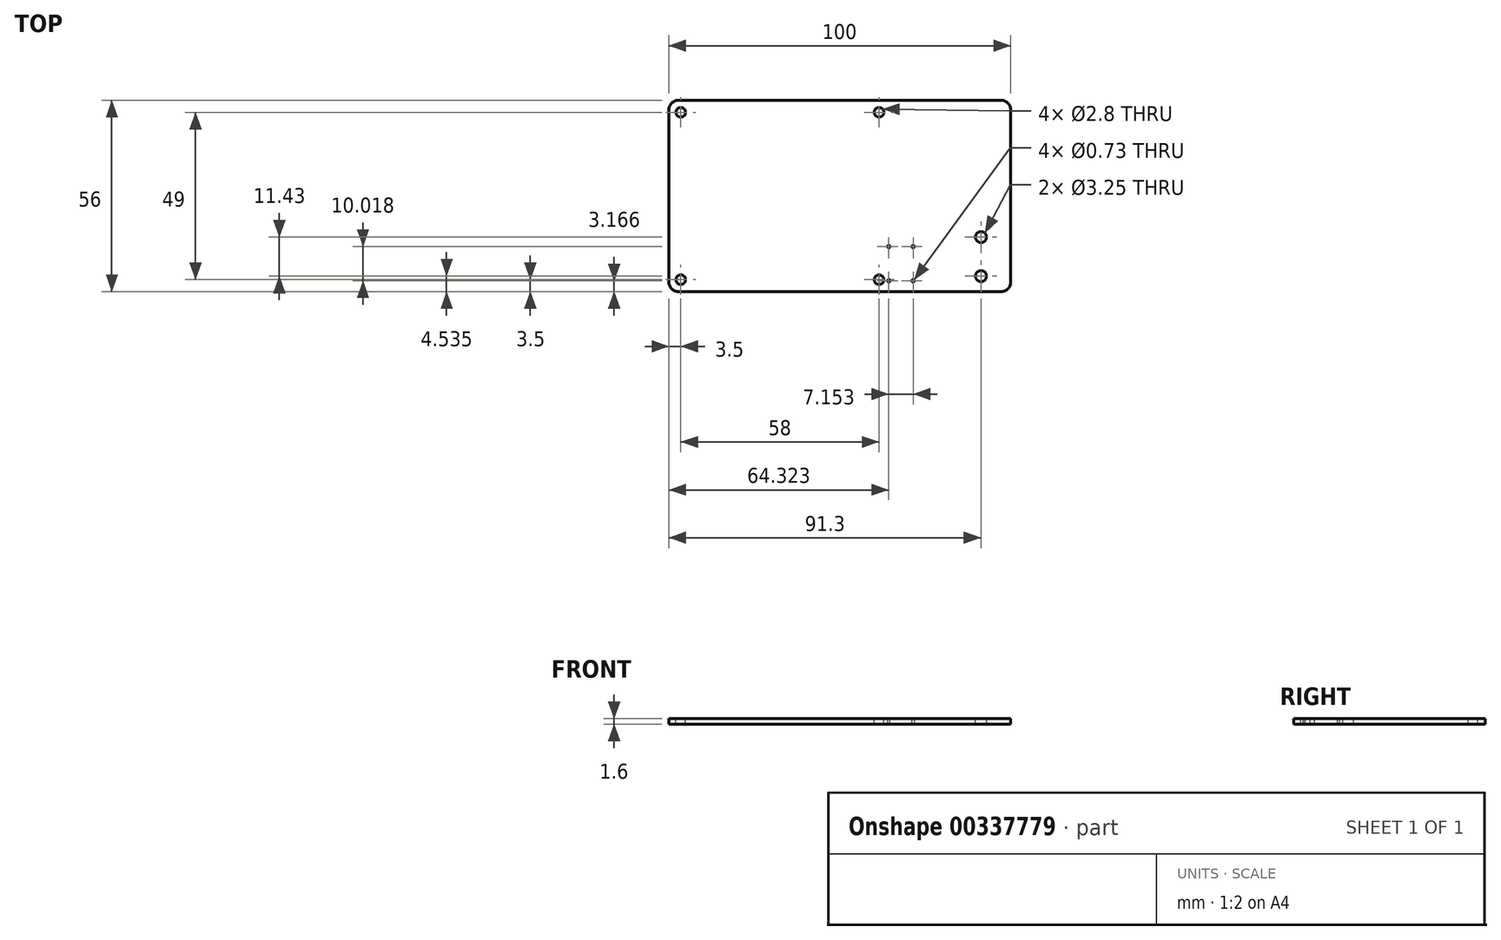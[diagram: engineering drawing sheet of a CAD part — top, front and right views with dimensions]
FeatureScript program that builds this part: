
annotation { "Feature Type Name" : "Feature", "Feature Type Description" : "" }
export const myFeature = defineFeature(function(context is Context, id is Id, definition is map)
    precondition{}
    {
        {
            var Q0;
            Q0=qCreatedBy(makeId("Top.planeOp"),FACE);
            var sketch = newSketch(context, id + "F0", { "sketchPlane" : qUnion([Q0])});
            skLineSegment(sketch, "E0.bottom", {"start": v(-57.5, 28) * mm, "end": v(42.5, 28) * mm});
            skLineSegment(sketch, "E0.top", {"start": v(-57.5, -28) * mm, "end": v(42.5, -28) * mm});
            skLineSegment(sketch, "E0.left", {"start": v(-57.5, 28) * mm, "end": v(-57.5, -28) * mm});
            skLineSegment(sketch, "E0.right", {"start": v(42.5, 28) * mm, "end": v(42.5, -28) * mm});
            skSolve(sketch);
        }
        {
            var Q0;
            Q0 = qSketchRegion(id + "F0", true);
            extrude(context, id + "F1", {"entities" : qUnion([Q0]), "depth" : 1.6 * mm});
        }
        {
            var Q0;
            Q0=makeQuery(id+"F1.opExtrude","CAP_FACE",FACE,{"disambiguationData":[OSD([sQuery(id+"F0.wireOp",EDGE,"E0.bottom"),sQuery(id+"F0.wireOp",EDGE,"E0.top"),sQuery(id+"F0.wireOp",EDGE,"E0.left"),sQuery(id+"F0.wireOp",EDGE,"E0.right")])],"isStart":false});
            var sketch = newSketch(context, id + "F2", { "sketchPlane" : qUnion([Q0])});
            skCircle(sketch, "E1", {"center": v(-54, 24.5) * mm, "radius": 1.4 * mm});
            skCircle(sketch, "E2.MirrorC", {"center": v(-54, -24.5) * mm, "radius": 1.4 * mm});
            skLineSegment(sketch, "E3", {"start": v(-25, 30.66) * mm, "end": v(-25, -34.31) * mm, "construction": true});
            skCircle(sketch, "E4.MirrorC", {"center": v(4, 24.5) * mm, "radius": 1.4 * mm});
            skCircle(sketch, "E5.MirrorC", {"center": v(4, -24.5) * mm, "radius": 1.4 * mm});
            skSolve(sketch);
        }
        {
            var Q0;
            Q0 = qSketchRegion(id + "F2", true);
            extrude(context, id + "F3", {"entities" : qUnion([Q0]), "operationType" : NewBodyOperationType.REMOVE, "endBound" : BoundingType.UP_TO_NEXT, "oppositeDirection" : true, "depth" : 25 * mm});
        }
        {
            var Q0;
            Q0=makeQuery(id+"F1.opExtrude","SWEPT_EDGE",EDGE,{"disambiguationData":[OSD([sQuery(id+"F0.wireOp",EDGE,"E0.bottom"),sQuery(id+"F0.wireOp",EDGE,"E0.left")])]});
            var Q1;
            Q1=makeQuery(id+"F1.opExtrude","SWEPT_EDGE",EDGE,{"disambiguationData":[OSD([sQuery(id+"F0.wireOp",EDGE,"E0.top"),sQuery(id+"F0.wireOp",EDGE,"E0.left")])]});
            var Q2;
            Q2=makeQuery(id+"F1.opExtrude","SWEPT_EDGE",EDGE,{"disambiguationData":[OSD([sQuery(id+"F0.wireOp",EDGE,"E0.bottom"),sQuery(id+"F0.wireOp",EDGE,"E0.right")])]});
            var Q3;
            Q3=makeQuery(id+"F1.opExtrude","SWEPT_EDGE",EDGE,{"disambiguationData":[OSD([sQuery(id+"F0.wireOp",EDGE,"E0.top"),sQuery(id+"F0.wireOp",EDGE,"E0.right")])]});
            fillet(context, id + "F4", {"entities" : qUnion([Q0, Q1, Q2, Q3]), "radius" : 2.8 * mm, "tangentPropagation" : true, "allowEdgeOverflow" : false});
        }
        {
            var Q0;
            Q0=makeQuery(id+"F1.opExtrude","CAP_FACE",FACE,{"disambiguationData":[OSD([sQuery(id+"F0.wireOp",EDGE,"E0.bottom"),sQuery(id+"F0.wireOp",EDGE,"E0.top"),sQuery(id+"F0.wireOp",EDGE,"E0.left"),sQuery(id+"F0.wireOp",EDGE,"E0.right")])],"isStart":false});
            var sketch = newSketch(context, id + "F5", { "sketchPlane" : qUnion([Q0])});
            skLineSegment(sketch, "E6.bottom", {"start": v(42.5, -25.7) * mm, "end": v(33.8, -25.7) * mm, "construction": true});
            skLineSegment(sketch, "E6.top", {"start": v(42.5, -23.46) * mm, "end": v(33.8, -23.46) * mm, "construction": true});
            skLineSegment(sketch, "E6.left", {"start": v(42.5, -25.7) * mm, "end": v(42.5, -23.46) * mm});
            skLineSegment(sketch, "E6.right", {"start": v(33.8, -25.7) * mm, "end": v(33.8, -23.46) * mm, "construction": true});
            skCircle(sketch, "E7", {"center": v(33.8, -23.46) * mm, "radius": 1.63 * mm});
            skCircle(sketch, "E8", {"center": v(33.8, -12.04) * mm, "radius": 1.63 * mm});
            skLineSegment(sketch, "E9", {"start": v(33.8, -23.46) * mm, "end": v(33.8, -12.04) * mm, "construction": true});
            skSolve(sketch);
        }
        {
            var Q0;
            Q0 = qSketchRegion(id + "F5", true);
            extrude(context, id + "F6", {"entities" : qUnion([Q0]), "operationType" : NewBodyOperationType.REMOVE, "endBound" : BoundingType.UP_TO_NEXT, "oppositeDirection" : true, "depth" : 25 * mm});
        }
        {
            var Q0;
            Q0=makeQuery(id+"F1.opExtrude","CAP_FACE",FACE,{"disambiguationData":[OSD([sQuery(id+"F0.wireOp",EDGE,"E0.bottom"),sQuery(id+"F0.wireOp",EDGE,"E0.top"),sQuery(id+"F0.wireOp",EDGE,"E0.left"),sQuery(id+"F0.wireOp",EDGE,"E0.right")])],"isStart":false});
            var sketch = newSketch(context, id + "F7", { "sketchPlane" : qUnion([Q0])});
            skLineSegment(sketch, "E10", {"start": v(42.5, -25.2) * mm, "end": v(14, -25.2) * mm, "construction": true});
            skCircle(sketch, "E11", {"center": v(13.98, -24.83) * mm, "radius": 0.37 * mm});
            skLineSegment(sketch, "E12", {"start": v(14, -25.2) * mm, "end": v(14, -14.45) * mm, "construction": true});
            skLineSegment(sketch, "E13", {"start": v(6.7, -19.83) * mm, "end": v(14, -19.83) * mm, "construction": true});
            skLineSegment(sketch, "E14", {"start": v(14, -25.2) * mm, "end": v(6.8, -25.2) * mm, "construction": true});
            skLineSegment(sketch, "E15", {"start": v(10.4, -25.2) * mm, "end": v(10.4, -14.47) * mm, "construction": true});
            skCircle(sketch, "E16.MirrorC", {"center": v(6.82, -24.83) * mm, "radius": 0.37 * mm});
            skCircle(sketch, "E17.MirrorC", {"center": v(13.98, -14.82) * mm, "radius": 0.37 * mm});
            skCircle(sketch, "E18.MirrorC", {"center": v(6.82, -14.82) * mm, "radius": 0.37 * mm});
            skSolve(sketch);
        }
        {
            var Q0;
            Q0 = qSketchRegion(id + "F7", true);
            extrude(context, id + "F8", {"entities" : qUnion([Q0]), "operationType" : NewBodyOperationType.REMOVE, "endBound" : BoundingType.THROUGH_ALL, "oppositeDirection" : true, "depth" : 25 * mm});
        }
    });
